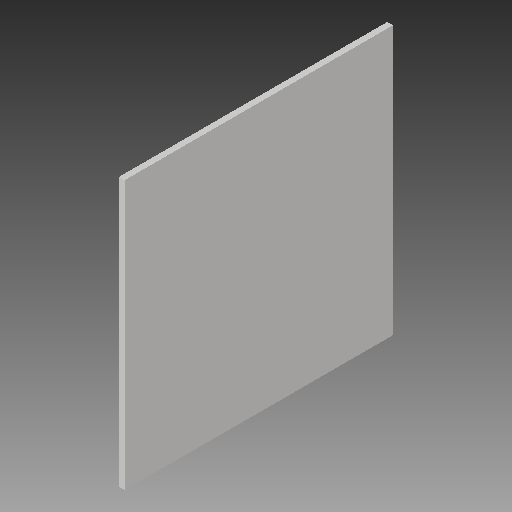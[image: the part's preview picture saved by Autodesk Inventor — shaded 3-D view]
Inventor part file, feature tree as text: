
AUTODESK INVENTOR PART (.ipt)
format: ipt  version: 2019 (Build 230136000, 136)  size: 90,624 bytes
history: native  units: mm
features: extrude x1, sketch x1
ambient origin geometry x8: Origin, YZ Plane, XZ Plane, XY Plane, X Axis, Y Axis, Z Axis, Center Point
bodies: Solid1 (feature_tree)
feature tree (2):
  extrude  "Extrusion1"  Depth=70.0mm
  sketch  "Sketch1"  dims[d0=70.0mm d1=70.0mm d2=35.0mm d3=35.0mm d4=1.5mm d5=0.0mm]
